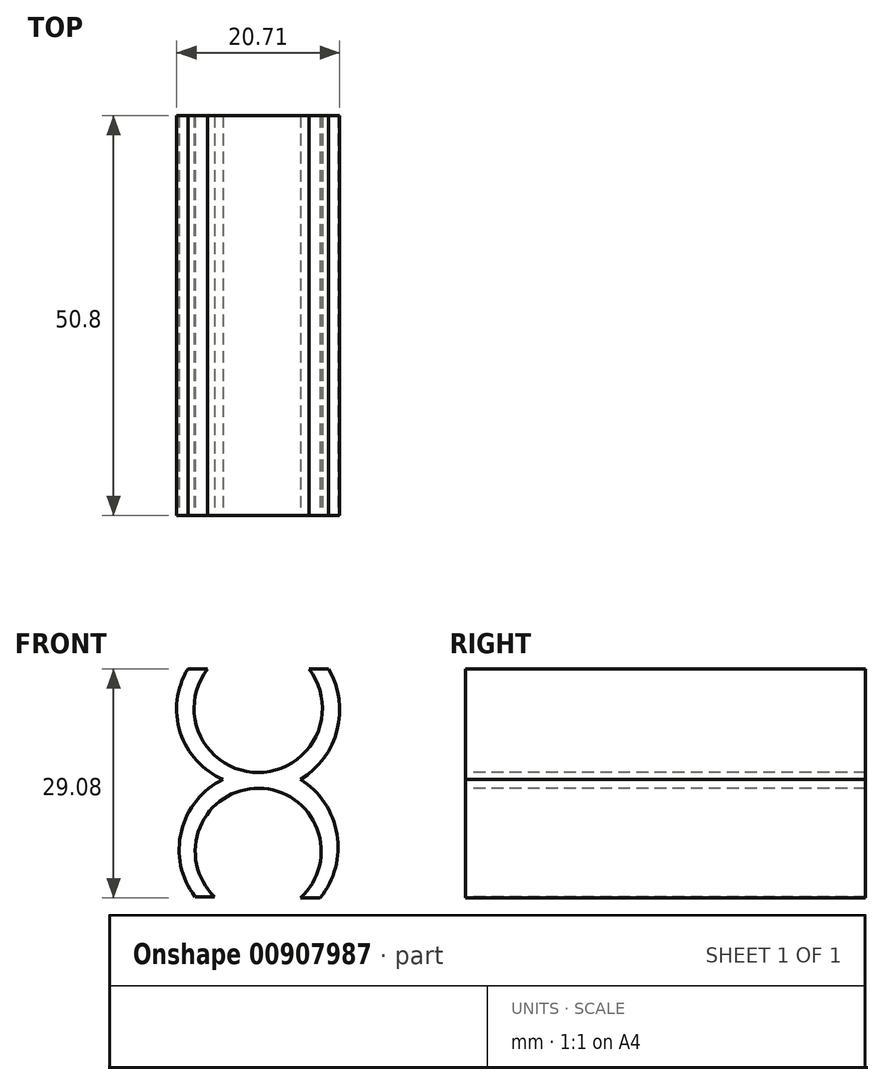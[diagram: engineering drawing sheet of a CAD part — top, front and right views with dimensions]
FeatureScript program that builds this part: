
annotation { "Feature Type Name" : "Feature", "Feature Type Description" : "" }
export const myFeature = defineFeature(function(context is Context, id is Id, definition is map)
    precondition{}
    {
        {
            var Q0;
            Q0=qCreatedBy(makeId("Top.planeOp"),FACE);
            var sketch = newSketch(context, id + "F0", { "sketchPlane" : qUnion([Q0])});
            skLineSegment(sketch, "E0.bottom", {"start": v(25.4, -25.4) * mm, "end": v(-25.4, -25.4) * mm});
            skLineSegment(sketch, "E0.top", {"start": v(25.4, 25.4) * mm, "end": v(-25.4, 25.4) * mm});
            skLineSegment(sketch, "E0.left", {"start": v(25.4, -25.4) * mm, "end": v(25.4, 25.4) * mm});
            skLineSegment(sketch, "E0.right", {"start": v(-25.4, -25.4) * mm, "end": v(-25.4, 25.4) * mm});
            skPoint(sketch, "E0.middle", {"position": v(0, 0) * mm});
            skSolve(sketch);
        }
        {
            var Q0;
            Q0 = qSketchRegion(id + "F0", true);
            extrude(context, id + "F1", {"entities" : qUnion([Q0]), "depth" : 50.8 * mm, "offsetDistance" : 25.4 * mm});
        }
        {
            var Q0;
            Q0=makeQuery(id+"F1.opExtrude","SWEPT_FACE",FACE,{"disambiguationData":[OSD([sQuery(id+"F0.wireOp",EDGE,"E0.bottom")])]});
            var sketch = newSketch(context, id + "F2", { "sketchPlane" : qUnion([Q0])});
            skLineSegment(sketch, "E1", {"start": v(0, 50.8) * mm, "end": v(0, 45.8) * mm});
            skCircle(sketch, "E2", {"center": v(0, 45.8) * mm, "radius": 8.15 * mm});
            skSolve(sketch);
        }
        {
            var Q0;
            {var subQ1=makeQuery(id+"F1.opExtrude","CAP_EDGE",EDGE,{"disambiguationData":[OSD([sQuery(id+"F0.wireOp",EDGE,"E0.bottom")])],"isStart":false});var subQ4=makeQuery(id+"F2.imprint","IMPRINT",VERTEX,{"derivedFrom":subQ1});Q0=makeQuery(id+"F2.imprint","IMPRINT",FACE,{"disambiguationData":[TD([[makeQuery(id+"F2.imprint","IMPRINT",EDGE,{"disambiguationData":[TD([[subQ4,1.0]])],"derivedFrom":subQ1}),1.0]])]});}
            extrude(context, id + "F3", {"entities" : qUnion([Q0]), "operationType" : NewBodyOperationType.REMOVE, "endBound" : BoundingType.UP_TO_NEXT, "oppositeDirection" : true, "depth" : 25.4 * mm, "offsetDistance" : 25.4 * mm});
        }
        {
            var Q0;
            Q0=makeQuery(id+"F1.opExtrude","SWEPT_FACE",FACE,{"disambiguationData":[OSD([sQuery(id+"F0.wireOp",EDGE,"E0.bottom")])]});
            var sketch = newSketch(context, id + "F4", { "sketchPlane" : qUnion([Q0])});
            skLineSegment(sketch, "E3", {"start": v(0, 37.65) * mm, "end": v(0, 35.65) * mm});
            skLineSegment(sketch, "E4", {"start": v(0, 35.65) * mm, "end": v(0, 27.65) * mm});
            skCircle(sketch, "E5", {"center": v(0, 27.65) * mm, "radius": 8 * mm});
            skLineSegment(sketch, "E6.bottom", {"start": v(-25.4, 0) * mm, "end": v(25.4, 0) * mm});
            skLineSegment(sketch, "E6.top", {"start": v(-25.4, 21.2) * mm, "end": v(25.4, 21.2) * mm});
            skLineSegment(sketch, "E6.left", {"start": v(-25.4, 0) * mm, "end": v(-25.4, 21.2) * mm});
            skLineSegment(sketch, "E6.right", {"start": v(25.4, 0) * mm, "end": v(25.4, 21.2) * mm});
            skSolve(sketch);
        }
        {
            var Q0;
            {var subQ0=sQuery(id+"F4.wireOp",EDGE,"E5");var subQ1=makeQuery(id+"F4.imprint","INTERSECT",VERTEX,{"derivedFrom":[sQuery(id+"F4.wireOp",EDGE,"E3"),subQ0]});Q0=makeQuery(id+"F4.imprint","IMPRINT",FACE,{"disambiguationData":[TD([[makeQuery(id+"F4.imprint","IMPRINT",EDGE,{"disambiguationData":[TD([[subQ1,-1.0]])],"derivedFrom":subQ0}),1.0]])]});}
            var Q1;
            Q1=makeQuery(id+"F4.imprint","IMPRINT",FACE,{"disambiguationData":[TD([[makeQuery(id+"F4.imprint","IMPRINT",EDGE,{"derivedFrom":sQuery(id+"F4.wireOp",EDGE,"E6.bottom")}),-1.0]])]});
            var Q2;
            {var subQ0=sQuery(id+"F4.wireOp",EDGE,"E6.top");var subQ1=sQuery(id+"F4.wireOp",EDGE,"E5");var subQ2=makeQuery(id+"F4.imprint","INTERSECT",VERTEX,{"disambiguationData":[OD(0.0)],"derivedFrom":[subQ1,subQ0]});Q2=makeQuery(id+"F4.imprint","IMPRINT",FACE,{"disambiguationData":[TD([[makeQuery(id+"F4.imprint","IMPRINT",EDGE,{"disambiguationData":[TD([[subQ2,-1.0]])],"derivedFrom":subQ1}),1.0]])]});}
            extrude(context, id + "F5", {"entities" : qUnion([Q0, Q1, Q2]), "operationType" : NewBodyOperationType.REMOVE, "endBound" : BoundingType.UP_TO_NEXT, "oppositeDirection" : true, "depth" : 25.4 * mm, "offsetDistance" : 25.4 * mm});
        }
        {
            var Q0;
            Q0=makeQuery(id+"F1.opExtrude","SWEPT_FACE",FACE,{"disambiguationData":[OSD([sQuery(id+"F0.wireOp",EDGE,"E0.bottom")])]});
            var sketch = newSketch(context, id + "F6", { "sketchPlane" : qUnion([Q0])});
            skLineSegment(sketch, "E7", {"start": v(-4.72, 21.2) * mm, "end": v(-5.87, 21.2) * mm});
            skLineSegment(sketch, "E8", {"start": v(-5.87, 21.2) * mm, "end": v(-5.54, 21.88) * mm});
            skLineSegment(sketch, "E9", {"start": v(-5.54, 21.88) * mm, "end": v(-4.72, 21.2) * mm});
            skLineSegment(sketch, "E10", {"start": v(4.72, 21.2) * mm, "end": v(5.79, 21.2) * mm});
            skLineSegment(sketch, "E11", {"start": v(5.79, 21.2) * mm, "end": v(5.25, 21.88) * mm});
            skPoint(sketch, "E11.endSnap0", {"position": v(5.25, 21.2) * mm});
            skLineSegment(sketch, "E12", {"start": v(5.25, 21.88) * mm, "end": v(4.72, 21.2) * mm});
            skSolve(sketch);
        }
        {
            var Q0;
            {var subQ0=sQuery(id+"F6.wireOp",EDGE,"E9");Q0=makeQuery(id+"F6.imprint","IMPRINT",FACE,{"disambiguationData":[TD([[makeQuery(id+"F6.imprint","IMPRINT",EDGE,{"derivedFrom":subQ0}),-1.0]])]});}
            var Q1;
            {var subQ0=sQuery(id+"F6.wireOp",EDGE,"E12");Q1=makeQuery(id+"F6.imprint","IMPRINT",FACE,{"disambiguationData":[TD([[makeQuery(id+"F6.imprint","IMPRINT",EDGE,{"derivedFrom":subQ0}),1.0]])]});}
            var Q2;
            {var subQ0=sQuery(id+"F6.wireOp",EDGE,"E10");Q2=makeQuery(id+"F6.imprint","IMPRINT",FACE,{"disambiguationData":[TD([[makeQuery(id+"F6.imprint","IMPRINT",EDGE,{"derivedFrom":subQ0}),1.0]])]});}
            var Q3;
            {var subQ0=sQuery(id+"F6.wireOp",EDGE,"E7");Q3=makeQuery(id+"F6.imprint","IMPRINT",FACE,{"disambiguationData":[TD([[makeQuery(id+"F6.imprint","IMPRINT",EDGE,{"derivedFrom":subQ0}),1.0]])]});}
            extrude(context, id + "F7", {"entities" : qUnion([Q0, Q1, Q2, Q3]), "operationType" : NewBodyOperationType.REMOVE, "endBound" : BoundingType.UP_TO_NEXT, "oppositeDirection" : true, "depth" : 25.4 * mm, "offsetDistance" : 25.4 * mm});
        }
        {
            var Q0;
            Q0=makeQuery(id+"F1.opExtrude","SWEPT_FACE",FACE,{"disambiguationData":[OSD([sQuery(id+"F0.wireOp",EDGE,"E0.bottom")])]});
            var sketch = newSketch(context, id + "F8", { "sketchPlane" : qUnion([Q0])});
            skLineSegment(sketch, "E13", {"start": v(-6.44, 50.8) * mm, "end": v(-8.94, 50.8) * mm});
            skLineSegment(sketch, "E14", {"start": v(6.44, 50.8) * mm, "end": v(8.94, 50.8) * mm});
            skLineSegment(sketch, "E15", {"start": v(-5.54, 21.88) * mm, "end": v(-8.04, 21.88) * mm});
            skLineSegment(sketch, "E16", {"start": v(5.37, 21.72) * mm, "end": v(7.87, 21.72) * mm});
            skArc(sketch, "E17", {"start": v(5.37, 36.77) * mm, "mid": v(10.03, 43.05) * mm, "end": v(8.94, 50.8) * mm});
            skArc(sketch, "E18", {"start": v(7.87, 21.72) * mm, "mid": v(10, 29.8) * mm, "end": v(5.37, 36.77) * mm});
            skArc(sketch, "E19", {"start": v(-8.94, 50.8) * mm, "mid": v(-9.9, 42.76) * mm, "end": v(-4.44, 36.77) * mm});
            skArc(sketch, "E20", {"start": v(-4.44, 36.77) * mm, "mid": v(-9.76, 30.18) * mm, "end": v(-8.04, 21.88) * mm});
            skSolve(sketch);
        }
        {
            var Q0;
            Q0=makeQuery(id+"F8.imprint","IMPRINT",FACE,{"disambiguationData":[TD([[makeQuery(id+"F8.imprint","IMPRINT",EDGE,{"derivedFrom":sQuery(id+"F8.wireOp",EDGE,"E15")}),1.0]])]});
            var Q1;
            Q1=makeQuery(id+"F8.imprint","IMPRINT",FACE,{"disambiguationData":[TD([[makeQuery(id+"F8.imprint","IMPRINT",EDGE,{"derivedFrom":sQuery(id+"F8.wireOp",EDGE,"E16")}),-1.0]])]});
            extrude(context, id + "F9", {"entities" : qUnion([Q0, Q1]), "operationType" : NewBodyOperationType.REMOVE, "endBound" : BoundingType.UP_TO_NEXT, "oppositeDirection" : true, "depth" : 25.4 * mm, "offsetDistance" : 25.4 * mm});
        }
    });
